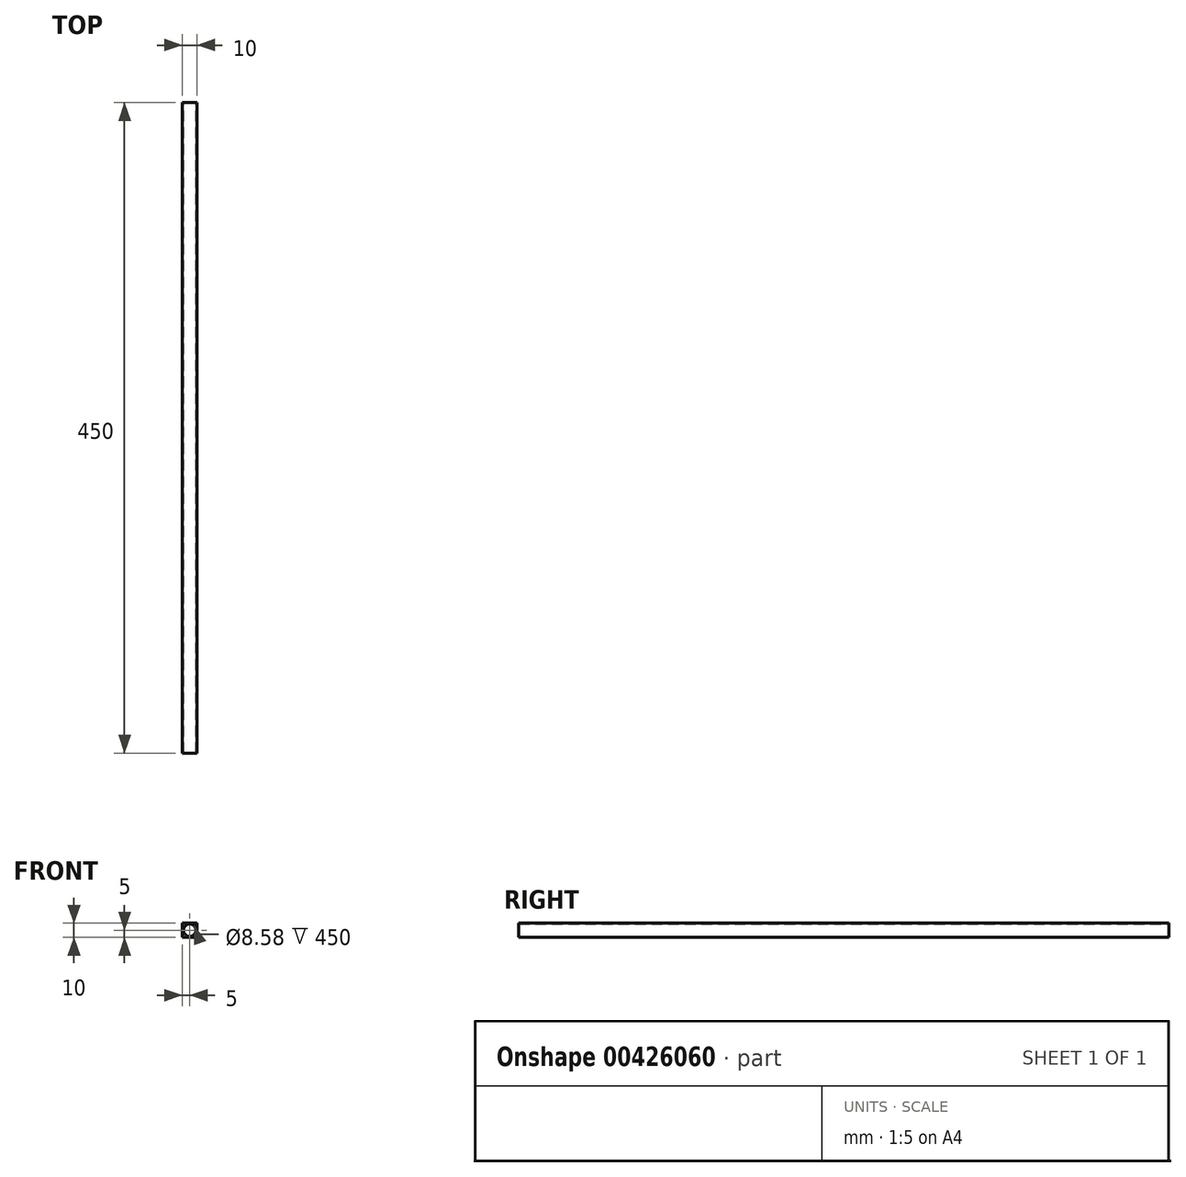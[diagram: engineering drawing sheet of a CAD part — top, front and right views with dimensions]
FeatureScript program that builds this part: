
annotation { "Feature Type Name" : "Feature", "Feature Type Description" : "" }
export const myFeature = defineFeature(function(context is Context, id is Id, definition is map)
    precondition{}
    {
        {
            var Q0;
            Q0=qCreatedBy(makeId("Front.planeOp"),FACE);
            var sketch = newSketch(context, id + "F0", { "sketchPlane" : qUnion([Q0])});
            skLineSegment(sketch, "E0.bottom", {"start": v(5, -5) * mm, "end": v(-5, -5) * mm});
            skLineSegment(sketch, "E0.top", {"start": v(5, 5) * mm, "end": v(-5, 5) * mm});
            skLineSegment(sketch, "E0.left", {"start": v(5, -5) * mm, "end": v(5, 5) * mm});
            skLineSegment(sketch, "E0.right", {"start": v(-5, -5) * mm, "end": v(-5, 5) * mm});
            skPoint(sketch, "E0.middle", {"position": v(0, 0) * mm});
            skCircle(sketch, "E1", {"center": v(0, 0) * mm, "radius": 4.29 * mm});
            skSolve(sketch);
        }
        {
            var Q0;
            Q0 = qSketchRegion(id + "F0", true);
            extrude(context, id + "F1", {"entities" : qUnion([Q0]), "depth" : 450 * mm});
        }
    });
